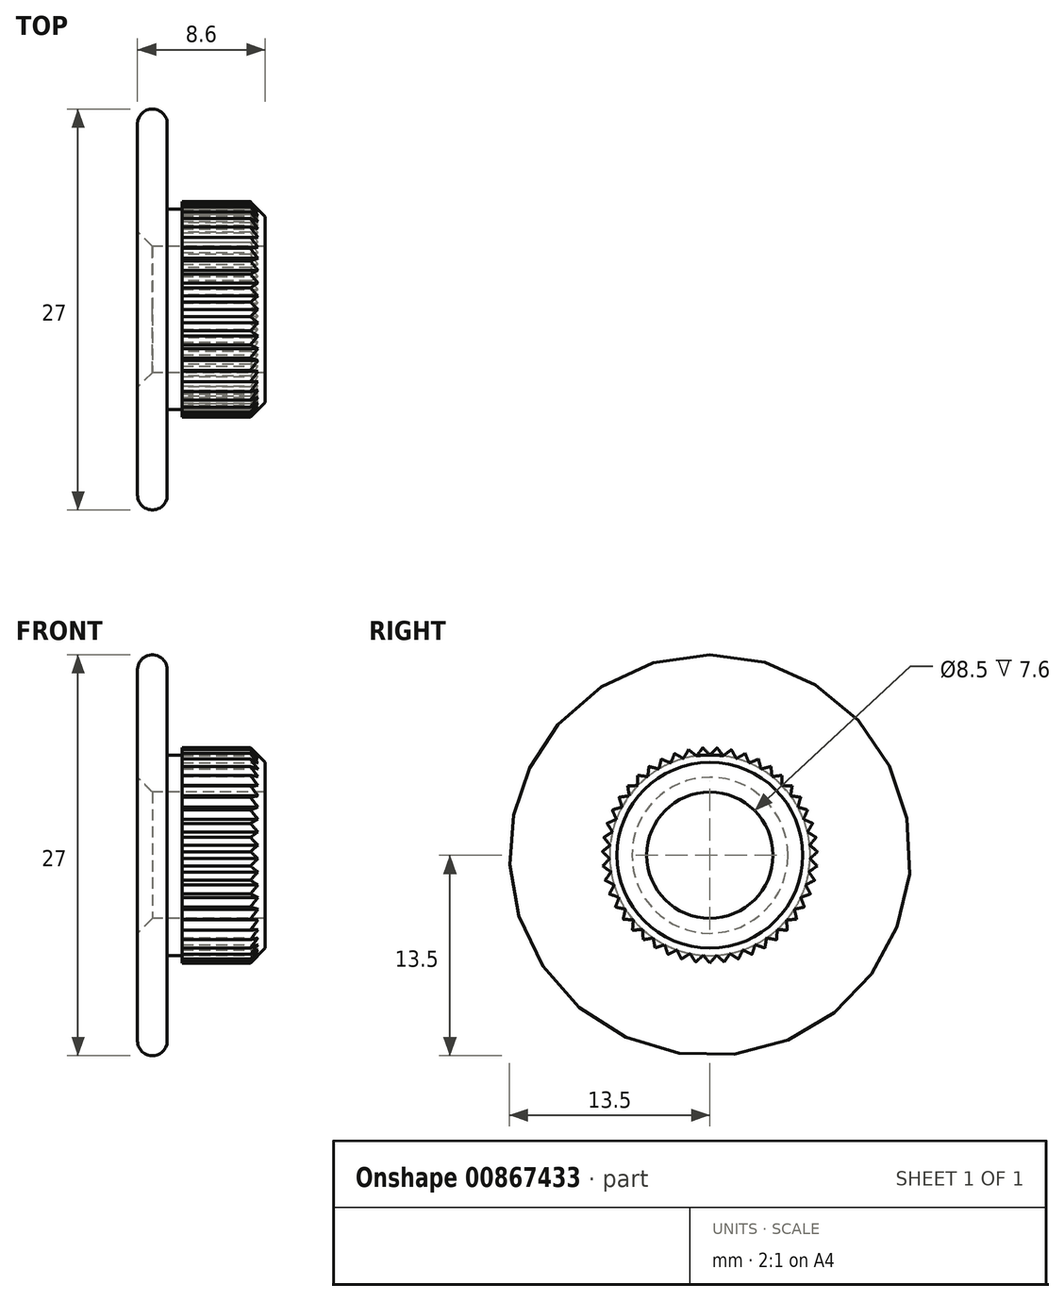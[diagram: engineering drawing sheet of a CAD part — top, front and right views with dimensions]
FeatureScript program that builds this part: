
annotation { "Feature Type Name" : "Feature", "Feature Type Description" : "" }
export const myFeature = defineFeature(function(context is Context, id is Id, definition is map)
    precondition{}
    {
        {
            var Q0;
            Q0=qCreatedBy(makeId("Front.planeOp"),FACE);
            var sketch = newSketch(context, id + "F0", { "sketchPlane" : qUnion([Q0])});
            skLineSegment(sketch, "E0", {"start": v(-4.3, 5.25) * mm, "end": v(-4.3, 12.5) * mm});
            skArc(sketch, "E1", {"start": v(-2.3, 12.5) * mm, "mid": v(-3.3, 13.5) * mm, "end": v(-4.3, 12.5) * mm});
            skLineSegment(sketch, "E2", {"start": v(-2.3, 12.5) * mm, "end": v(-2.3, 6.75) * mm});
            skLineSegment(sketch, "E3", {"start": v(-2.3, 6.75) * mm, "end": v(-1.3, 6.75) * mm});
            skLineSegment(sketch, "E4", {"start": v(-1.3, 6.75) * mm, "end": v(-1.3, 7.25) * mm});
            skLineSegment(sketch, "E5", {"start": v(-1.3, 7.25) * mm, "end": v(3.3, 7.25) * mm});
            skLineSegment(sketch, "E6", {"start": v(3.3, 7.25) * mm, "end": v(4.3, 6.25) * mm});
            skLineSegment(sketch, "E7", {"start": v(4.3, 6.25) * mm, "end": v(4.3, 4.25) * mm});
            skLineSegment(sketch, "E8", {"start": v(4.3, 4.25) * mm, "end": v(-3.3, 4.25) * mm});
            skLineSegment(sketch, "E9", {"start": v(-4.3, 5.25) * mm, "end": v(-3.3, 4.25) * mm});
            skSolve(sketch);
        }
        {
            var Q0;
            Q0=qCreatedBy(makeId("Front.planeOp"),FACE);
            var sketch = newSketch(context, id + "F1", { "sketchPlane" : qUnion([Q0])});
            skLineSegment(sketch, "E10", {"start": v(-17.42, 0) * mm, "end": v(19.2, 0) * mm});
            skSolve(sketch);
        }
        {
            var Q0;
            Q0 = qSketchRegion(id + "F0", true);
            var Q1;
            Q1=sQuery(id+"F1.wireOp",EDGE,"E10");
            revolve(context, id + "F2", {"surfaceOperationType" : NewSurfaceOperationType.NEW, "entities" : qUnion([Q0]), "axis" : qUnion([Q1]), "revolveType" : RevolveType.FULL});
        }
        {
            var Q0;
            Q0=makeQuery(id+"F2.opRevolve","SWEPT_FACE",FACE,{"disambiguationData":[OSD([sQuery(id+"F0.wireOp",EDGE,"E7")])]});
            var sketch = newSketch(context, id + "F3", { "sketchPlane" : qUnion([Q0])});
            skLineSegment(sketch, "E11", {"start": v(-0.5, 7.25) * mm, "end": v(0.5, 7.25) * mm});
            skLineSegment(sketch, "E12", {"start": v(0.5, 7.25) * mm, "end": v(0, 6.75) * mm});
            skLineSegment(sketch, "E13", {"start": v(0, 6.75) * mm, "end": v(-0.5, 7.25) * mm});
            skLineSegment(sketch, "E14.1.0", {"start": v(-0.9, 6.69) * mm, "end": v(-1.46, 7.12) * mm});
            skLineSegment(sketch, "E14.1.1", {"start": v(-1.46, 7.12) * mm, "end": v(-0.47, 7.25) * mm});
            skLineSegment(sketch, "E14.1.2", {"start": v(-0.47, 7.25) * mm, "end": v(-0.9, 6.69) * mm});
            skLineSegment(sketch, "E14.2.0", {"start": v(-1.78, 6.51) * mm, "end": v(-2.4, 6.86) * mm});
            skLineSegment(sketch, "E14.2.1", {"start": v(-2.4, 6.86) * mm, "end": v(-1.43, 7.12) * mm});
            skLineSegment(sketch, "E14.2.2", {"start": v(-1.43, 7.12) * mm, "end": v(-1.78, 6.51) * mm});
            skLineSegment(sketch, "E14.3.0", {"start": v(-2.64, 6.21) * mm, "end": v(-3.3, 6.48) * mm});
            skLineSegment(sketch, "E14.3.1", {"start": v(-3.3, 6.48) * mm, "end": v(-2.37, 6.87) * mm});
            skLineSegment(sketch, "E14.3.2", {"start": v(-2.37, 6.87) * mm, "end": v(-2.64, 6.21) * mm});
            skLineSegment(sketch, "E14.4.0", {"start": v(-3.44, 5.8) * mm, "end": v(-4.12, 5.98) * mm});
            skLineSegment(sketch, "E14.4.1", {"start": v(-4.12, 5.98) * mm, "end": v(-3.26, 6.5) * mm});
            skLineSegment(sketch, "E14.4.2", {"start": v(-3.26, 6.5) * mm, "end": v(-3.44, 5.8) * mm});
            skLineSegment(sketch, "E14.5.0", {"start": v(-4.18, 5.3) * mm, "end": v(-4.89, 5.38) * mm});
            skLineSegment(sketch, "E14.5.1", {"start": v(-4.89, 5.38) * mm, "end": v(-4.1, 6) * mm});
            skLineSegment(sketch, "E14.5.2", {"start": v(-4.1, 6) * mm, "end": v(-4.18, 5.3) * mm});
            skLineSegment(sketch, "E14.6.0", {"start": v(-4.85, 4.7) * mm, "end": v(-5.56, 4.68) * mm});
            skLineSegment(sketch, "E14.6.1", {"start": v(-5.56, 4.68) * mm, "end": v(-4.86, 5.4) * mm});
            skLineSegment(sketch, "E14.6.2", {"start": v(-4.86, 5.4) * mm, "end": v(-4.85, 4.7) * mm});
            skLineSegment(sketch, "E14.7.0", {"start": v(-5.43, 4) * mm, "end": v(-6.13, 3.9) * mm});
            skLineSegment(sketch, "E14.7.1", {"start": v(-6.13, 3.9) * mm, "end": v(-5.54, 4.7) * mm});
            skLineSegment(sketch, "E14.7.2", {"start": v(-5.54, 4.7) * mm, "end": v(-5.43, 4) * mm});
            skLineSegment(sketch, "E14.8.0", {"start": v(-5.92, 3.24) * mm, "end": v(-6.6, 3.05) * mm});
            skLineSegment(sketch, "E14.8.1", {"start": v(-6.6, 3.05) * mm, "end": v(-6.12, 3.92) * mm});
            skLineSegment(sketch, "E14.8.2", {"start": v(-6.12, 3.92) * mm, "end": v(-5.92, 3.24) * mm});
            skLineSegment(sketch, "E14.9.0", {"start": v(-6.3, 2.43) * mm, "end": v(-6.95, 2.14) * mm});
            skLineSegment(sketch, "E14.9.1", {"start": v(-6.95, 2.14) * mm, "end": v(-6.59, 3.07) * mm});
            skLineSegment(sketch, "E14.9.2", {"start": v(-6.59, 3.07) * mm, "end": v(-6.3, 2.43) * mm});
            skLineSegment(sketch, "E14.10.0", {"start": v(-6.57, 1.56) * mm, "end": v(-7.17, 1.2) * mm});
            skLineSegment(sketch, "E14.10.1", {"start": v(-7.17, 1.2) * mm, "end": v(-6.94, 2.17) * mm});
            skLineSegment(sketch, "E14.10.2", {"start": v(-6.94, 2.17) * mm, "end": v(-6.57, 1.56) * mm});
            skLineSegment(sketch, "E14.11.0", {"start": v(-6.72, 0.68) * mm, "end": v(-7.26, 0.23) * mm});
            skLineSegment(sketch, "E14.11.1", {"start": v(-7.26, 0.23) * mm, "end": v(-7.16, 1.22) * mm});
            skLineSegment(sketch, "E14.11.2", {"start": v(-7.16, 1.22) * mm, "end": v(-6.72, 0.68) * mm});
            skLineSegment(sketch, "E14.12.0", {"start": v(-6.75, -0.23) * mm, "end": v(-7.23, -0.74) * mm});
            skLineSegment(sketch, "E14.12.1", {"start": v(-7.23, -0.74) * mm, "end": v(-7.26, 0.26) * mm});
            skLineSegment(sketch, "E14.12.2", {"start": v(-7.26, 0.26) * mm, "end": v(-6.75, -0.23) * mm});
            skLineSegment(sketch, "E14.13.0", {"start": v(-6.66, -1.12) * mm, "end": v(-7.07, -1.7) * mm});
            skLineSegment(sketch, "E14.13.1", {"start": v(-7.07, -1.7) * mm, "end": v(-7.23, -0.71) * mm});
            skLineSegment(sketch, "E14.13.2", {"start": v(-7.23, -0.71) * mm, "end": v(-6.66, -1.12) * mm});
            skLineSegment(sketch, "E14.14.0", {"start": v(-6.45, -2) * mm, "end": v(-6.78, -2.63) * mm});
            skLineSegment(sketch, "E14.14.1", {"start": v(-6.78, -2.63) * mm, "end": v(-7.07, -1.67) * mm});
            skLineSegment(sketch, "E14.14.2", {"start": v(-7.07, -1.67) * mm, "end": v(-6.45, -2) * mm});
            skLineSegment(sketch, "E14.15.0", {"start": v(-6.12, -2.84) * mm, "end": v(-6.37, -3.5) * mm});
            skLineSegment(sketch, "E14.15.1", {"start": v(-6.37, -3.5) * mm, "end": v(-6.79, -2.6) * mm});
            skLineSegment(sketch, "E14.15.2", {"start": v(-6.79, -2.6) * mm, "end": v(-6.12, -2.84) * mm});
            skLineSegment(sketch, "E14.16.0", {"start": v(-5.69, -3.63) * mm, "end": v(-5.84, -4.32) * mm});
            skLineSegment(sketch, "E14.16.1", {"start": v(-5.84, -4.32) * mm, "end": v(-6.38, -3.48) * mm});
            skLineSegment(sketch, "E14.16.2", {"start": v(-6.38, -3.48) * mm, "end": v(-5.69, -3.63) * mm});
            skLineSegment(sketch, "E14.17.0", {"start": v(-5.15, -4.36) * mm, "end": v(-5.21, -5.06) * mm});
            skLineSegment(sketch, "E14.17.1", {"start": v(-5.21, -5.06) * mm, "end": v(-5.86, -4.3) * mm});
            skLineSegment(sketch, "E14.17.2", {"start": v(-5.86, -4.3) * mm, "end": v(-5.15, -4.36) * mm});
            skLineSegment(sketch, "E14.18.0", {"start": v(-4.53, -5) * mm, "end": v(-4.5, -5.71) * mm});
            skLineSegment(sketch, "E14.18.1", {"start": v(-4.5, -5.71) * mm, "end": v(-5.23, -5.04) * mm});
            skLineSegment(sketch, "E14.18.2", {"start": v(-5.23, -5.04) * mm, "end": v(-4.53, -5) * mm});
            skLineSegment(sketch, "E14.19.0", {"start": v(-3.82, -5.56) * mm, "end": v(-3.7, -6.26) * mm});
            skLineSegment(sketch, "E14.19.1", {"start": v(-3.7, -6.26) * mm, "end": v(-4.52, -5.7) * mm});
            skLineSegment(sketch, "E14.19.2", {"start": v(-4.52, -5.7) * mm, "end": v(-3.82, -5.56) * mm});
            skLineSegment(sketch, "E14.20.0", {"start": v(-3.04, -6.02) * mm, "end": v(-2.82, -6.7) * mm});
            skLineSegment(sketch, "E14.20.1", {"start": v(-2.82, -6.7) * mm, "end": v(-3.72, -6.25) * mm});
            skLineSegment(sketch, "E14.20.2", {"start": v(-3.72, -6.25) * mm, "end": v(-3.04, -6.02) * mm});
            skLineSegment(sketch, "E14.21.0", {"start": v(-2.21, -6.38) * mm, "end": v(-1.9, -7.01) * mm});
            skLineSegment(sketch, "E14.21.1", {"start": v(-1.9, -7.01) * mm, "end": v(-2.85, -6.68) * mm});
            skLineSegment(sketch, "E14.21.2", {"start": v(-2.85, -6.68) * mm, "end": v(-2.21, -6.38) * mm});
            skLineSegment(sketch, "E14.22.0", {"start": v(-1.34, -6.61) * mm, "end": v(-0.95, -7.2) * mm});
            skLineSegment(sketch, "E14.22.1", {"start": v(-0.95, -7.2) * mm, "end": v(-1.93, -7) * mm});
            skLineSegment(sketch, "E14.22.2", {"start": v(-1.93, -7) * mm, "end": v(-1.34, -6.61) * mm});
            skLineSegment(sketch, "E14.23.0", {"start": v(-0.45, -6.73) * mm, "end": v(0.01, -7.27) * mm});
            skLineSegment(sketch, "E14.23.1", {"start": v(0.01, -7.27) * mm, "end": v(-0.98, -7.2) * mm});
            skLineSegment(sketch, "E14.23.2", {"start": v(-0.98, -7.2) * mm, "end": v(-0.45, -6.73) * mm});
            skLineSegment(sketch, "E14.24.0", {"start": v(0.45, -6.73) * mm, "end": v(0.98, -7.2) * mm});
            skLineSegment(sketch, "E14.24.1", {"start": v(0.98, -7.2) * mm, "end": v(-0.01, -7.27) * mm});
            skLineSegment(sketch, "E14.24.2", {"start": v(-0.01, -7.27) * mm, "end": v(0.45, -6.73) * mm});
            skLineSegment(sketch, "E14.25.0", {"start": v(1.34, -6.61) * mm, "end": v(1.93, -7) * mm});
            skLineSegment(sketch, "E14.25.1", {"start": v(1.93, -7) * mm, "end": v(0.95, -7.2) * mm});
            skLineSegment(sketch, "E14.25.2", {"start": v(0.95, -7.2) * mm, "end": v(1.34, -6.61) * mm});
            skLineSegment(sketch, "E14.26.0", {"start": v(2.21, -6.38) * mm, "end": v(2.85, -6.68) * mm});
            skLineSegment(sketch, "E14.26.1", {"start": v(2.85, -6.68) * mm, "end": v(1.9, -7.01) * mm});
            skLineSegment(sketch, "E14.26.2", {"start": v(1.9, -7.01) * mm, "end": v(2.21, -6.38) * mm});
            skLineSegment(sketch, "E14.27.0", {"start": v(3.04, -6.02) * mm, "end": v(3.72, -6.25) * mm});
            skLineSegment(sketch, "E14.27.1", {"start": v(3.72, -6.25) * mm, "end": v(2.82, -6.7) * mm});
            skLineSegment(sketch, "E14.27.2", {"start": v(2.82, -6.7) * mm, "end": v(3.04, -6.02) * mm});
            skLineSegment(sketch, "E14.28.0", {"start": v(3.82, -5.56) * mm, "end": v(4.52, -5.7) * mm});
            skLineSegment(sketch, "E14.28.1", {"start": v(4.52, -5.7) * mm, "end": v(3.7, -6.26) * mm});
            skLineSegment(sketch, "E14.28.2", {"start": v(3.7, -6.26) * mm, "end": v(3.82, -5.56) * mm});
            skLineSegment(sketch, "E14.29.0", {"start": v(4.53, -5) * mm, "end": v(5.23, -5.04) * mm});
            skLineSegment(sketch, "E14.29.1", {"start": v(5.23, -5.04) * mm, "end": v(4.5, -5.71) * mm});
            skLineSegment(sketch, "E14.29.2", {"start": v(4.5, -5.71) * mm, "end": v(4.53, -5) * mm});
            skLineSegment(sketch, "E14.30.0", {"start": v(5.15, -4.36) * mm, "end": v(5.86, -4.3) * mm});
            skLineSegment(sketch, "E14.30.1", {"start": v(5.86, -4.3) * mm, "end": v(5.21, -5.06) * mm});
            skLineSegment(sketch, "E14.30.2", {"start": v(5.21, -5.06) * mm, "end": v(5.15, -4.36) * mm});
            skLineSegment(sketch, "E14.31.0", {"start": v(5.69, -3.63) * mm, "end": v(6.38, -3.48) * mm});
            skLineSegment(sketch, "E14.31.1", {"start": v(6.38, -3.48) * mm, "end": v(5.84, -4.32) * mm});
            skLineSegment(sketch, "E14.31.2", {"start": v(5.84, -4.32) * mm, "end": v(5.69, -3.63) * mm});
            skLineSegment(sketch, "E14.32.0", {"start": v(6.12, -2.84) * mm, "end": v(6.79, -2.6) * mm});
            skLineSegment(sketch, "E14.32.1", {"start": v(6.79, -2.6) * mm, "end": v(6.37, -3.5) * mm});
            skLineSegment(sketch, "E14.32.2", {"start": v(6.37, -3.5) * mm, "end": v(6.12, -2.84) * mm});
            skLineSegment(sketch, "E14.33.0", {"start": v(6.45, -2) * mm, "end": v(7.07, -1.67) * mm});
            skLineSegment(sketch, "E14.33.1", {"start": v(7.07, -1.67) * mm, "end": v(6.78, -2.63) * mm});
            skLineSegment(sketch, "E14.33.2", {"start": v(6.78, -2.63) * mm, "end": v(6.45, -2) * mm});
            skLineSegment(sketch, "E14.34.0", {"start": v(6.66, -1.12) * mm, "end": v(7.23, -0.71) * mm});
            skLineSegment(sketch, "E14.34.1", {"start": v(7.23, -0.71) * mm, "end": v(7.07, -1.7) * mm});
            skLineSegment(sketch, "E14.34.2", {"start": v(7.07, -1.7) * mm, "end": v(6.66, -1.12) * mm});
            skLineSegment(sketch, "E14.35.0", {"start": v(6.75, -0.23) * mm, "end": v(7.26, 0.26) * mm});
            skLineSegment(sketch, "E14.35.1", {"start": v(7.26, 0.26) * mm, "end": v(7.23, -0.74) * mm});
            skLineSegment(sketch, "E14.35.2", {"start": v(7.23, -0.74) * mm, "end": v(6.75, -0.23) * mm});
            skLineSegment(sketch, "E14.36.0", {"start": v(6.72, 0.68) * mm, "end": v(7.16, 1.22) * mm});
            skLineSegment(sketch, "E14.36.1", {"start": v(7.16, 1.22) * mm, "end": v(7.26, 0.23) * mm});
            skLineSegment(sketch, "E14.36.2", {"start": v(7.26, 0.23) * mm, "end": v(6.72, 0.68) * mm});
            skLineSegment(sketch, "E14.37.0", {"start": v(6.57, 1.56) * mm, "end": v(6.94, 2.17) * mm});
            skLineSegment(sketch, "E14.37.1", {"start": v(6.94, 2.17) * mm, "end": v(7.17, 1.2) * mm});
            skLineSegment(sketch, "E14.37.2", {"start": v(7.17, 1.2) * mm, "end": v(6.57, 1.56) * mm});
            skLineSegment(sketch, "E14.38.0", {"start": v(6.3, 2.43) * mm, "end": v(6.59, 3.07) * mm});
            skLineSegment(sketch, "E14.38.1", {"start": v(6.59, 3.07) * mm, "end": v(6.95, 2.14) * mm});
            skLineSegment(sketch, "E14.38.2", {"start": v(6.95, 2.14) * mm, "end": v(6.3, 2.43) * mm});
            skLineSegment(sketch, "E14.39.0", {"start": v(5.92, 3.24) * mm, "end": v(6.12, 3.92) * mm});
            skLineSegment(sketch, "E14.39.1", {"start": v(6.12, 3.92) * mm, "end": v(6.6, 3.05) * mm});
            skLineSegment(sketch, "E14.39.2", {"start": v(6.6, 3.05) * mm, "end": v(5.92, 3.24) * mm});
            skLineSegment(sketch, "E14.40.0", {"start": v(5.43, 4) * mm, "end": v(5.54, 4.7) * mm});
            skLineSegment(sketch, "E14.40.1", {"start": v(5.54, 4.7) * mm, "end": v(6.13, 3.9) * mm});
            skLineSegment(sketch, "E14.40.2", {"start": v(6.13, 3.9) * mm, "end": v(5.43, 4) * mm});
            skLineSegment(sketch, "E14.41.0", {"start": v(4.85, 4.7) * mm, "end": v(4.86, 5.4) * mm});
            skLineSegment(sketch, "E14.41.1", {"start": v(4.86, 5.4) * mm, "end": v(5.56, 4.68) * mm});
            skLineSegment(sketch, "E14.41.2", {"start": v(5.56, 4.68) * mm, "end": v(4.85, 4.7) * mm});
            skLineSegment(sketch, "E14.42.0", {"start": v(4.18, 5.3) * mm, "end": v(4.1, 6) * mm});
            skLineSegment(sketch, "E14.42.1", {"start": v(4.1, 6) * mm, "end": v(4.89, 5.38) * mm});
            skLineSegment(sketch, "E14.42.2", {"start": v(4.89, 5.38) * mm, "end": v(4.18, 5.3) * mm});
            skPoint(sketch, "E14.center", {"position": v(0, 0) * mm});
            skLineSegment(sketch, "E15.1.43.0", {"start": v(3.44, 5.8) * mm, "end": v(3.26, 6.5) * mm});
            skLineSegment(sketch, "E15.3.43.0", {"start": v(3.26, 6.5) * mm, "end": v(4.12, 5.98) * mm});
            skLineSegment(sketch, "E15.6.43.0", {"start": v(4.12, 5.98) * mm, "end": v(3.44, 5.8) * mm});
            skLineSegment(sketch, "E16.1.44.0", {"start": v(2.64, 6.21) * mm, "end": v(2.37, 6.87) * mm});
            skLineSegment(sketch, "E16.3.44.0", {"start": v(2.37, 6.87) * mm, "end": v(3.3, 6.48) * mm});
            skLineSegment(sketch, "E16.6.44.0", {"start": v(3.3, 6.48) * mm, "end": v(2.64, 6.21) * mm});
            skLineSegment(sketch, "E17.1.45.0", {"start": v(1.78, 6.51) * mm, "end": v(1.43, 7.12) * mm});
            skLineSegment(sketch, "E17.3.45.0", {"start": v(1.43, 7.12) * mm, "end": v(2.4, 6.86) * mm});
            skLineSegment(sketch, "E17.6.45.0", {"start": v(2.4, 6.86) * mm, "end": v(1.78, 6.51) * mm});
            skLineSegment(sketch, "E18.1.46.0", {"start": v(0.9, 6.69) * mm, "end": v(0.47, 7.25) * mm});
            skLineSegment(sketch, "E18.3.46.0", {"start": v(0.47, 7.25) * mm, "end": v(1.46, 7.12) * mm});
            skLineSegment(sketch, "E18.6.46.0", {"start": v(1.46, 7.12) * mm, "end": v(0.9, 6.69) * mm});
            skSolve(sketch);
        }
        {
            var Q0;
            Q0 = qSketchRegion(id + "F3", true);
            var Q1;
            Q1=makeQuery(id+"F2.opRevolve","SWEPT_FACE",FACE,{"disambiguationData":[OSD([sQuery(id+"F0.wireOp",EDGE,"E4")])]});
            extrude(context, id + "F4", {"entities" : qUnion([Q0]), "operationType" : NewBodyOperationType.REMOVE, "endBound" : BoundingType.UP_TO_SURFACE, "oppositeDirection" : true, "depth" : 25 * mm, "endBoundEntityFace" : qUnion([Q1]), "offsetDistance" : 25 * mm});
        }
    });
